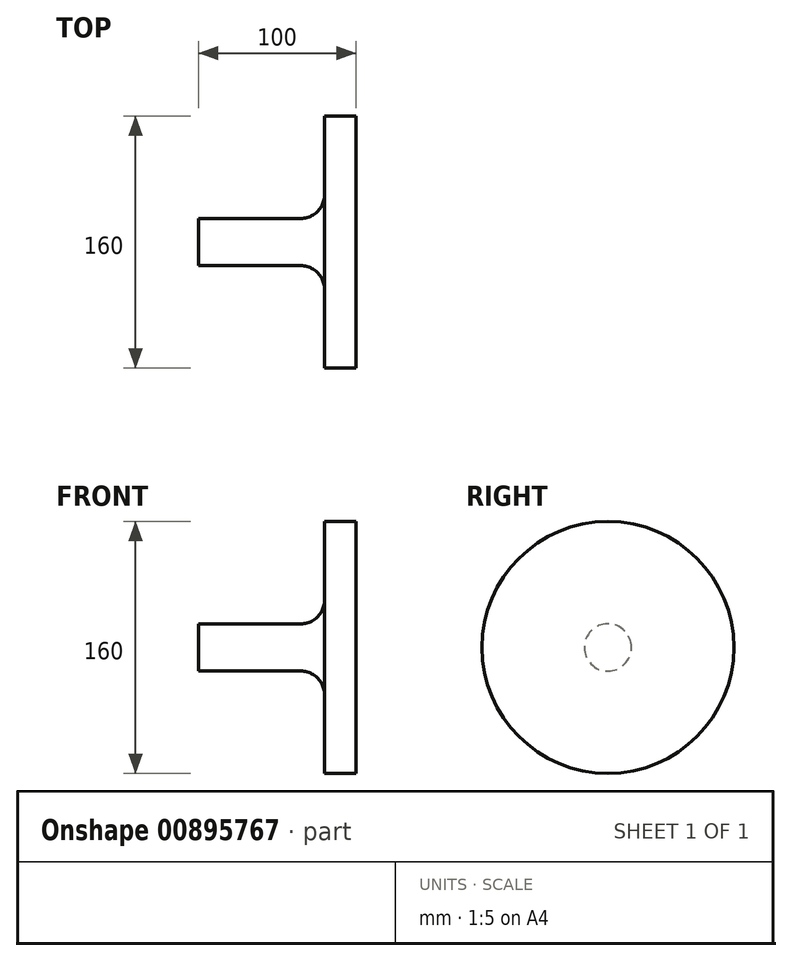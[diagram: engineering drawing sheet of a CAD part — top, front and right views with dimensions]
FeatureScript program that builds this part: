
annotation { "Feature Type Name" : "Feature", "Feature Type Description" : "" }
export const myFeature = defineFeature(function(context is Context, id is Id, definition is map)
    precondition{}
    {
        {
            var Q0;
            Q0=qCreatedBy(makeId("Front.planeOp"),FACE);
            var sketch = newSketch(context, id + "F0", { "sketchPlane" : qUnion([Q0])});
            skLineSegment(sketch, "E0", {"start": v(0, 15) * mm, "end": v(0, 0) * mm});
            skLineSegment(sketch, "E1", {"start": v(0, 0) * mm, "end": v(100, 0) * mm});
            skLineSegment(sketch, "E2", {"start": v(100, 0) * mm, "end": v(100, 80) * mm});
            skLineSegment(sketch, "E3", {"start": v(100, 80) * mm, "end": v(80, 80) * mm});
            skLineSegment(sketch, "E4", {"start": v(80, 80) * mm, "end": v(80, 30) * mm});
            skLineSegment(sketch, "E5", {"start": v(65, 15) * mm, "end": v(0, 15) * mm});
            skLineSegment(sketch, "E6", {"start": v(-69.83, 0) * mm, "end": v(107.22, 0) * mm, "construction": true});
            skPoint(sketch, "E7.visualSharp", {"position": v(80, 15) * mm});
            skArc(sketch, "E7.filletArc", {"start": v(65, 15) * mm, "mid": v(75.6, 19.4) * mm, "end": v(80, 30) * mm});
            skSolve(sketch);
        }
        {
            var Q0;
            Q0 = qSketchRegion(id + "F0", true);
            var Q1;
            Q1=sQuery(id+"F0.wireOp",EDGE,"E6");
            revolve(context, id + "F1", {"surfaceOperationType" : NewSurfaceOperationType.NEW, "entities" : qUnion([Q0]), "axis" : qUnion([Q1]), "revolveType" : RevolveType.FULL});
        }
    });
